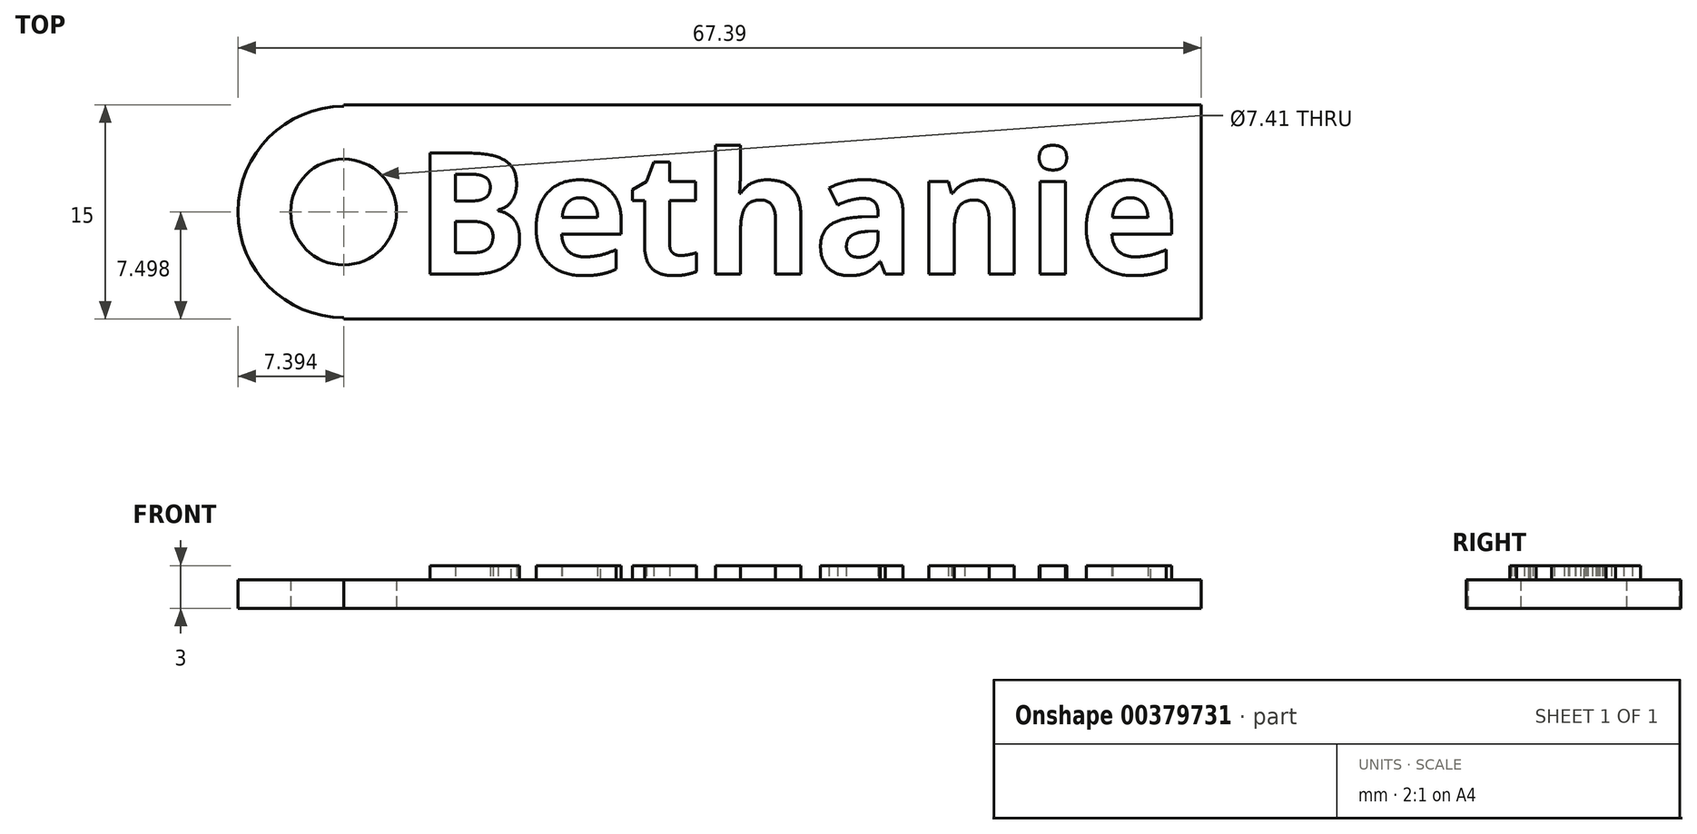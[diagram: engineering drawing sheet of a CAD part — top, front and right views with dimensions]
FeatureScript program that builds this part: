
annotation { "Feature Type Name" : "Feature", "Feature Type Description" : "" }
export const myFeature = defineFeature(function(context is Context, id is Id, definition is map)
    precondition{}
    {
        {
            var Q0;
            Q0=qCreatedBy(makeId("Top.planeOp"),FACE);
            var sketch = newSketch(context, id + "F0", { "sketchPlane" : qUnion([Q0])});
            skLineSegment(sketch, "E0.bottom", {"start": v(-15.77, -4.86) * mm, "end": v(44.23, -4.86) * mm});
            skLineSegment(sketch, "E0.top", {"start": v(-15.77, -19.86) * mm, "end": v(44.23, -19.86) * mm});
            skLineSegment(sketch, "E0.left", {"start": v(-15.77, -4.86) * mm, "end": v(-15.77, -4.97) * mm});
            skLineSegment(sketch, "E0.right", {"start": v(44.23, -4.86) * mm, "end": v(44.23, -19.86) * mm});
            skArc(sketch, "E1", {"start": v(-15.77, -4.97) * mm, "mid": v(-23.16, -12.36) * mm, "end": v(-15.77, -19.75) * mm});
            skLineSegment(sketch, "E2.trimOffspring", {"start": v(-15.77, -19.75) * mm, "end": v(-15.77, -19.86) * mm});
            skCircle(sketch, "E3", {"center": v(-15.77, -12.36) * mm, "radius": 3.7 * mm});
            skSolve(sketch);
        }
        {
            var Q0;
            Q0=makeQuery(id+"F0.imprint","IMPRINT",FACE,{"disambiguationData":[TD([[makeQuery(id+"F0.imprint","IMPRINT",EDGE,{"derivedFrom":sQuery(id+"F0.wireOp",EDGE,"E0.bottom")}),-1.0]])]});
            extrude(context, id + "F1", {"entities" : qUnion([Q0]), "depth" : 2 * mm});
        }
        {
            var Q0;
            Q0=makeQuery(id+"F1.opExtrude","CAP_FACE",FACE,{"disambiguationData":[OSD([sQuery(id+"F0.wireOp",EDGE,"E0.bottom"),sQuery(id+"F0.wireOp",EDGE,"E0.top"),sQuery(id+"F0.wireOp",EDGE,"E0.left"),sQuery(id+"F0.wireOp",EDGE,"E0.right"),sQuery(id+"F0.wireOp",EDGE,"E1"),sQuery(id+"F0.wireOp",EDGE,"E2.trimOffspring"),sQuery(id+"F0.wireOp",EDGE,"E3")])],"isStart":false});
            var sketch = newSketch(context, id + "F2", { "sketchPlane" : qUnion([Q0])});
            skText(sketch, "E4", { "text": "Bethanie", "fontName": "OpenSans-Bold.ttf"});
            const initialGuessF2  = {"E4": [-0.01079, -0.0167, 1, 0, 0.00853]};
            skSetInitialGuess(sketch, initialGuessF2);
            skSolve(sketch);
        }
        {
            var Q0;
            Q0 = qSketchRegion(id + "F2", true);
            extrude(context, id + "F3", {"entities" : qUnion([Q0]), "operationType" : NewBodyOperationType.ADD, "depth" : 1 * mm});
        }
    });
